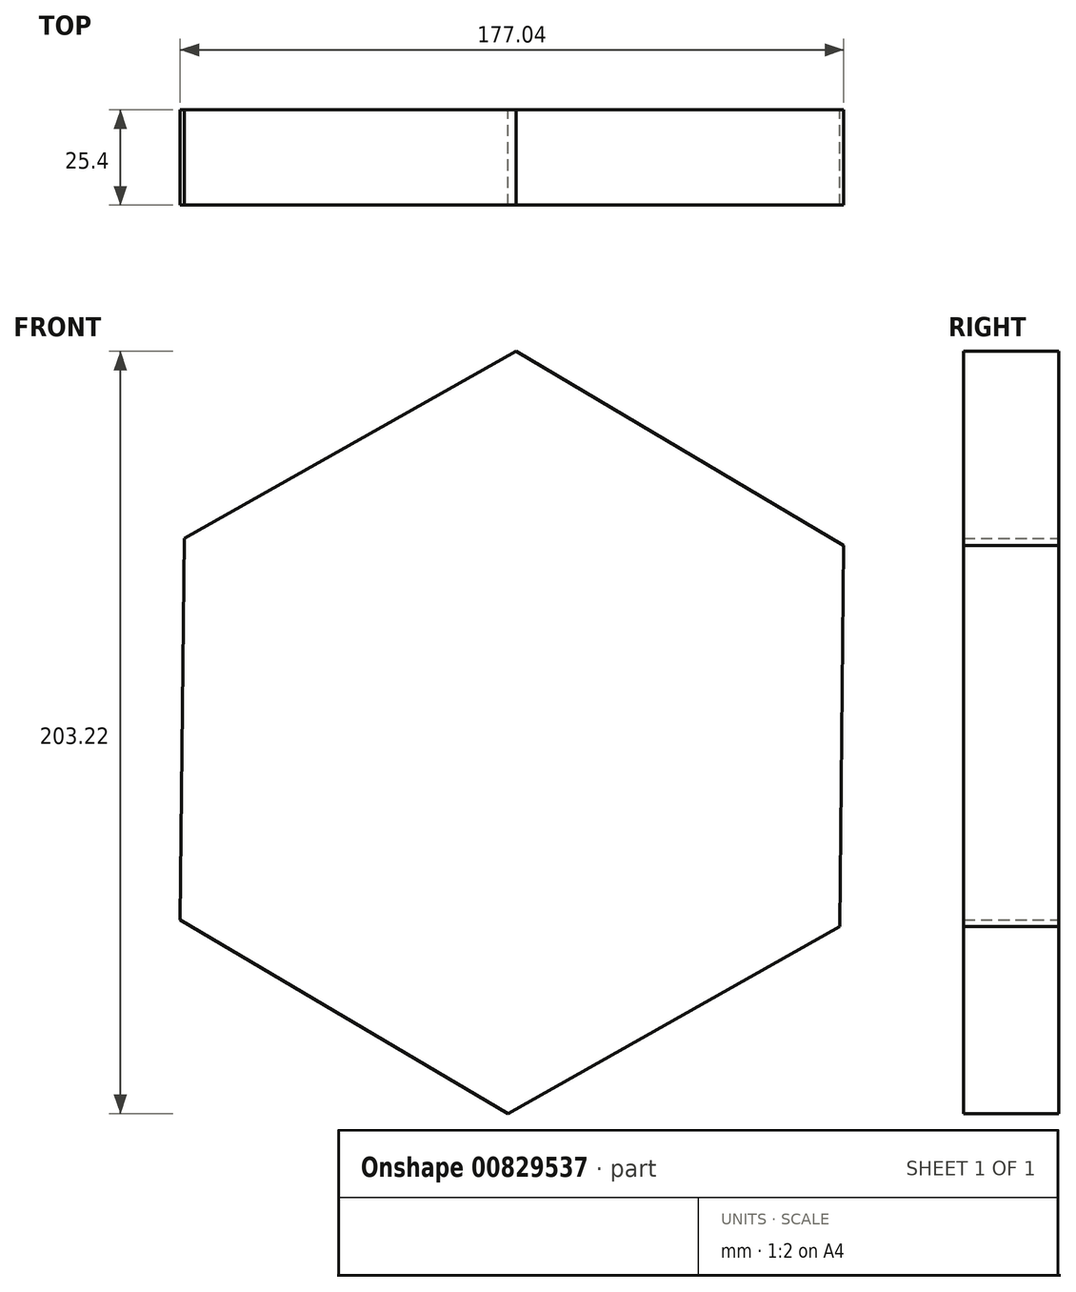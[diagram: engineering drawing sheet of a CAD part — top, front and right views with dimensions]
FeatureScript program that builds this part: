
annotation { "Feature Type Name" : "Feature", "Feature Type Description" : "" }
export const myFeature = defineFeature(function(context is Context, id is Id, definition is map)
    precondition{}
    {
        {
            var Q0;
            Q0=qCreatedBy(makeId("Front.planeOp"),FACE);
            var sketch = newSketch(context, id + "F0", { "sketchPlane" : qUnion([Q0])});
            skCircle(sketch, "E0.cCircle", {"center": v(0, 0) * mm, "radius": 88 * mm, "construction": true});
            skLineSegment(sketch, "E0.0", {"start": v(-1.04, -101.61) * mm, "end": v(-88.52, -49.9) * mm});
            skLineSegment(sketch, "E0.1", {"start": v(-88.52, -49.9) * mm, "end": v(-87.48, 51.7) * mm});
            skLineSegment(sketch, "E0.2", {"start": v(-87.48, 51.7) * mm, "end": v(1.04, 101.61) * mm});
            skLineSegment(sketch, "E0.3", {"start": v(1.04, 101.61) * mm, "end": v(88.52, 49.9) * mm});
            skLineSegment(sketch, "E0.4", {"start": v(88.52, 49.9) * mm, "end": v(87.48, -51.7) * mm});
            skLineSegment(sketch, "E0.5", {"start": v(87.48, -51.7) * mm, "end": v(-1.04, -101.61) * mm});
            skPoint(sketch, "E0.0.midPoint", {"position": v(-44.78, -75.76) * mm});
            skSolve(sketch);
        }
        {
            var Q0;
            Q0=makeQuery(id+"F0.imprint","IMPRINT",FACE,{"disambiguationData":[TD([[makeQuery(id+"F0.imprint","IMPRINT",EDGE,{"derivedFrom":sQuery(id+"F0.wireOp",EDGE,"E0.0")}),-1.0]])]});
            extrude(context, id + "F1", {"entities" : qUnion([Q0]), "depth" : 25.4 * mm, "offsetDistance" : 25.4 * mm});
        }
    });
